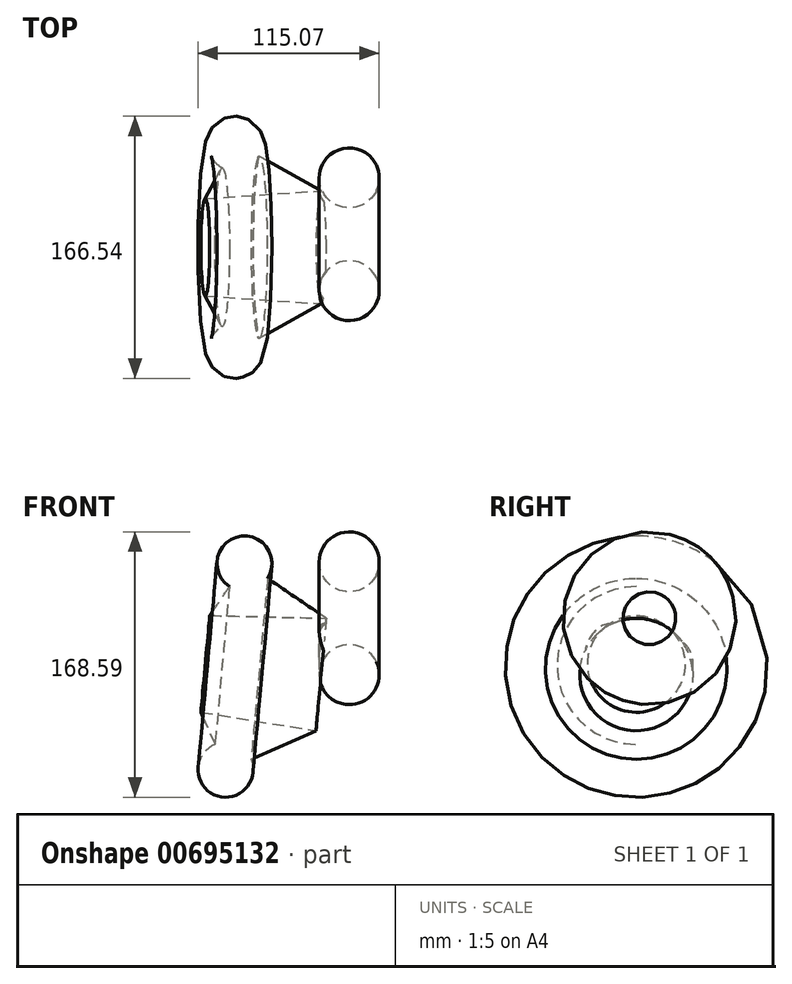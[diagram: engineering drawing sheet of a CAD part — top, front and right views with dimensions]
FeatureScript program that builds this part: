
annotation { "Feature Type Name" : "Feature", "Feature Type Description" : "" }
export const myFeature = defineFeature(function(context is Context, id is Id, definition is map)
    precondition{}
    {
        {
            var Q0;
            Q0=qCreatedBy(makeId("Top.planeOp"),FACE);
            var sketch = newSketch(context, id + "F0", { "sketchPlane" : qUnion([Q0])});
            skCircle(sketch, "E0", {"center": v(14.56, -27.53) * mm, "radius": 19.05 * mm});
            skLineSegment(sketch, "E1", {"start": v(39.03, 8.3) * mm, "end": v(4.66, 8.3) * mm});
            skSolve(sketch);
        }
        {
            var Q0;
            Q0=makeQuery(id+"F0.imprint","IMPRINT",FACE,{"disambiguationData":[TD([[makeQuery(id+"F0.imprint","IMPRINT",EDGE,{"derivedFrom":sQuery(id+"F0.wireOp",EDGE,"E0")}),1.0]])]});
            var Q1;
            Q1=sQuery(id+"F0.wireOp",EDGE,"E1");
            revolve(context, id + "F1", {"entities" : qUnion([Q0]), "axis" : qUnion([Q1]), "revolveType" : RevolveType.FULL});
        }
        {
            var Q0;
            Q0=qCreatedBy(makeId("Front.planeOp"),FACE);
            var sketch = newSketch(context, id + "F2", { "sketchPlane" : qUnion([Q0])});
            skCircle(sketch, "E2", {"center": v(-52, 34.79) * mm, "radius": 17.49 * mm});
            skSolve(sketch);
        }
        {
            var Q0;
            Q0=qCreatedBy(makeId("Front.planeOp"),FACE);
            var sketch = newSketch(context, id + "F3", { "sketchPlane" : qUnion([Q0])});
            skLineSegment(sketch, "E3", {"start": v(-51.43, 34.97) * mm, "end": v(0, 0) * mm});
            skLineSegment(sketch, "E4", {"start": v(-51.43, 34.97) * mm, "end": v(-74.04, 1.73) * mm});
            skLineSegment(sketch, "E5", {"start": v(-74.04, 1.73) * mm, "end": v(0, 0) * mm});
            skLineSegment(sketch, "E6", {"start": v(-58.76, -30.65) * mm, "end": v(-25.86, -33.66) * mm});
            skSolve(sketch);
        }
        {
            var Q0;
            Q0=makeQuery(id+"F3.imprint","IMPRINT",FACE,{"disambiguationData":[TD([[makeQuery(id+"F3.imprint","IMPRINT",EDGE,{"derivedFrom":sQuery(id+"F3.wireOp",EDGE,"E3")}),-1.0]])]});
            var Q1;
            Q1=makeQuery(id+"F2.imprint","IMPRINT",FACE,{"disambiguationData":[TD([[makeQuery(id+"F2.imprint","IMPRINT",EDGE,{"derivedFrom":sQuery(id+"F2.wireOp",EDGE,"E2")}),1.0]])]});
            var Q2;
            Q2=sQuery(id+"F3.wireOp",EDGE,"E6");
            revolve(context, id + "F4", {"operationType" : NewBodyOperationType.ADD, "entities" : qUnion([Q0, Q1]), "axis" : qUnion([Q2]), "revolveType" : RevolveType.FULL});
        }
    });
